# Revit family: VRIF-4104_1x4
name_source: partatom
category: Lighting Fixtures
units: mm (PartAtom-declared; Revit-internal decimal feet)

## family parameters
Always vertical = Yes
Cut with Voids When Loaded = No
Host = Ceiling
Light Source = Yes
OmniClass Number = 23.80.70.11.14.17
OmniClass Title = Direct/Indirect
Part Type = Normal
Room Calculation Point = No
Round Connector Dimension = Use Diameter
Shared = No

## types (2) — shared parameters
Color Filter = 16777215
Description = LED Vandal Resistant Recessed Flanged Ceiling Inset Door
Dimming Lamp Color Temperature Shift = <None>
Emit Shape Visible in Rendering = No
Emit from Rectangle Length = 4' - 0 5/16"
Emit from Rectangle Width = 1' - 0 11/32"
Housing Finish = Metal - Viscor - White
Inner Diffuser = Acrylic - Viscor - Frosted Round
Lamp = LED
Length = 4' - 0 5/16"
Lens Flat = Acrylic - Viscor - Clear Lens
Manufacturer = Certolux By Viscor
Model = VRIF-4104
Tilt Angle = 90.00°
URL = https://www.viscor.com
Voltage = 120 V
Width = 1' - 0 11/32"

## per-type parameters (varying)
| type | Apparent Load | Lamp Wattage | Photometric Web File |
| VRIF-4104-1X4-LED840K033LUNV | 31 VA | 31 VA | VRIF-4104-1X4-LED840K033LUNV.ies |
| VRIF-4104-1X4-LED840K039LUNV | 39 VA | 39 VA | VRIF-4104-1X4-LED840K039LUNV.ies |

## geometry (parser evidence)
native form markers: Sweep x3
no freeform markers — native parametric forms only
